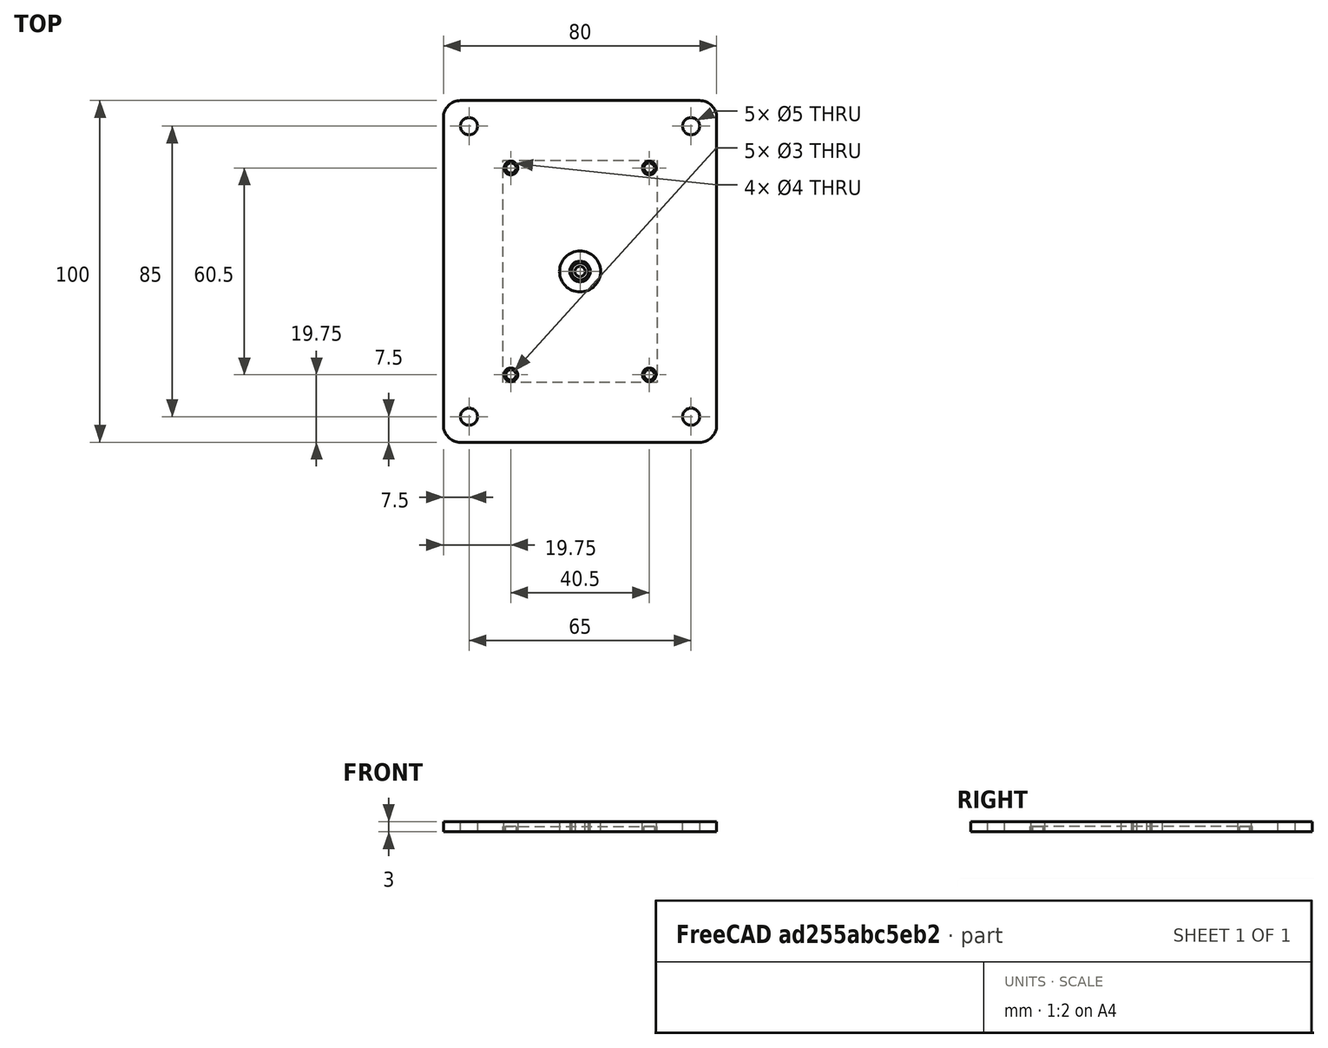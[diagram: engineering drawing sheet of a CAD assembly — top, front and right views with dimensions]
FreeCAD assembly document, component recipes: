
FREECAD ASSEMBLY — COMPONENT RECIPES ("ttgo_esp32_poe_mounting_plate")

This assembly document has 4 components, labeled P0..P3 below (a component is one placed body or linked part). 4 of them carry a construction recipe — the FreeCAD feature program that regenerates the part from scratch, quoted from this document or its linked companion documents; the rest are supplied as boundary geometry only. No exploded tour is included for this assembly.
COMPONENT P0 — recipe-attached ("Mounting Panel", modeled in this document).
Construction recipe (the document's own serialized feature program — sketch geometry with constraints, then the solid features built on it; lengths are millimeters unless a unit is written):

FEATURE [Sketcher::SketchObject] Sketch
  FullyConstrained = true
  MapMode = 5
  Support = -> [XY_Plane002]
  sketch-geometry (12):
    g0: LineSegment StartX=-40 StartY=50 StartZ=0 EndX=40 EndY=50 EndZ=0
    g1: LineSegment StartX=40 StartY=50 StartZ=0 EndX=40 EndY=-50 EndZ=0
    g2: LineSegment StartX=40 StartY=-50 StartZ=0 EndX=-40 EndY=-50 EndZ=0
    g3: LineSegment StartX=-40 StartY=-50 StartZ=0 EndX=-40 EndY=50 EndZ=0
    g4: LineSegment StartX=-35 StartY=50 StartZ=0 EndX=35 EndY=50 EndZ=0
    g5: LineSegment StartX=40 StartY=45 StartZ=0 EndX=40 EndY=-45 EndZ=0
    g6: LineSegment StartX=35 StartY=-50 StartZ=0 EndX=-35 EndY=-50 EndZ=0
    g7: LineSegment StartX=-40 StartY=-45 StartZ=0 EndX=-40 EndY=45 EndZ=0
    g8: ArcOfCircle CenterX=-35 CenterY=45 CenterZ=0 NormalX=0 NormalY=0 NormalZ=1 AngleXU=0 Radius=5 StartAngle=1.5708 EndAngle=3.14159
    g9: ArcOfCircle CenterX=35 CenterY=45 CenterZ=0 NormalX=0 NormalY=0 NormalZ=1 AngleXU=0 Radius=5 StartAngle=0 EndAngle=1.5708
    g10: ArcOfCircle CenterX=35 CenterY=-45 CenterZ=0 NormalX=0 NormalY=0 NormalZ=1 AngleXU=0 Radius=5 StartAngle=4.71239 EndAngle=6.28319
    g11: ArcOfCircle CenterX=-35 CenterY=-45 CenterZ=0 NormalX=0 NormalY=0 NormalZ=1 AngleXU=0 Radius=5 StartAngle=3.14159 EndAngle=4.71239
  constraints (30):
    c: Coincident(g0,g1)
    c: Coincident(g1,g2)
    c: Coincident(g2,g3)
    c: Coincident(g3,g0)
    c: Horizontal(g2)
    c: Vertical(g3)
    c: Symmetric(g0,g0,g-2)
    c: Symmetric(g0,g1,g-1)
    c: DistanceX(g0,g0) = 80
    c: DistanceY(g1,g1) = 100
    c: Horizontal(g4)
    c: Horizontal(g6)
    c: Vertical(g5)
    c: Vertical(g7)
    c: Tangent(g4,g8) = 1.5708
    c: Tangent(g7,g8) = 1.5708
    c: Tangent(g4,g9) = 1.5708
    c: Tangent(g5,g9) = 1.5708
    c: Tangent(g5,g10) = 1.5708
    c: Tangent(g6,g10) = 1.5708
    c: Tangent(g7,g11) = 1.5708
    c: Tangent(g6,g11) = 1.5708
    c: PointOnObject(g4,g0)
    c: PointOnObject(g7,g3)
    c: PointOnObject(g5,g1)
    c: PointOnObject(g6,g2)
    c: Equal(g8,g9)
    c: Equal(g9,g11)
    c: Equal(g11,g10)
    c: Radius(g11) = 5
FEATURE [PartDesign::Plane] DatumPlane001
  AttachmentOffset = pos=(0,0,3) rot=(0,0,1;0rad)
  Length = 97.8885
  MapMode = 5
  Placement = pos=(0,0,3) rot=(0,0,1;0rad)
  ResizeMode = 0
  Support = -> [XY_Plane002]
  Width = 117.889
FEATURE [PartDesign::Pad] Pad001
  Direction = (0,0,1)
  Length = 10
  Length2 = 10
  Profile = -> Sketch
  ReferenceAxis = -> Sketch [N_Axis]
  Type = 3
  UpToFace = -> DatumPlane001 [Plane]
FEATURE [Sketcher::SketchObject] Sketch003
  FullyConstrained = true
  MapMode = 5
  Placement = pos=(0,0,3) rot=(0,0,1;0rad)
  Support = -> [DatumPlane001]
  sketch-geometry (8):
    g0: LineSegment StartX=-20.25 StartY=30.25 StartZ=0 EndX=20.25 EndY=30.25 EndZ=0
    g1: LineSegment StartX=20.25 StartY=30.25 StartZ=0 EndX=20.25 EndY=-30.25 EndZ=0
    g2: LineSegment StartX=20.25 StartY=-30.25 StartZ=0 EndX=-20.25 EndY=-30.25 EndZ=0
    g3: LineSegment StartX=-20.25 StartY=-30.25 StartZ=0 EndX=-20.25 EndY=30.25 EndZ=0
    g4: Circle CenterX=-20.25 CenterY=30.25 CenterZ=0 NormalX=0 NormalY=0 NormalZ=1 AngleXU=0 Radius=2
    g5: Circle CenterX=20.25 CenterY=30.25 CenterZ=0 NormalX=0 NormalY=0 NormalZ=1 AngleXU=0 Radius=2
    g6: Circle CenterX=-20.25 CenterY=-30.25 CenterZ=0 NormalX=0 NormalY=0 NormalZ=1 AngleXU=0 Radius=2
    g7: Circle CenterX=20.25 CenterY=-30.25 CenterZ=0 NormalX=0 NormalY=0 NormalZ=1 AngleXU=0 Radius=2
  constraints (18):
    c: Coincident(g0,g1)
    c: Coincident(g1,g2)
    c: Coincident(g2,g3)
    c: Coincident(g3,g0)
    c: Horizontal(g2)
    c: Vertical(g3)
    c: Coincident(g4,g0)
    c: Coincident(g5,g0)
    c: Coincident(g6,g2)
    c: Coincident(g7,g1)
    c: Equal(g4,g5)
    c: Equal(g5,g6)
    c: Equal(g6,g7)
    c: Diameter(g6) = 4
    c: Symmetric(g4,g5,g-2)
    c: Symmetric(g5,g7,g-1)
    c: DistanceX(g0,g0) = 40.5
    c: DistanceY(g1,g1) = 60.5
FEATURE [PartDesign::Pocket] Pocket001
  BaseFeature = -> Pad001
  Direction = (0,0,-1)
  Length = 0
  Length2 = 5
  Profile = -> Sketch003
  ReferenceAxis = -> Sketch003 [N_Axis]
  Type = 3
  UpToFace = -> XY_Plane002
FEATURE [PartDesign::CoordinateSystem] Local_CS001  label="Mounting Panel Body Lower Left TTGO Board Mounting Hole"
  AttacherType = Attacher::AttachEngine3D
  MapMode = 45
  Placement = pos=(-20.25,-30.25,3) rot=(0,0,-1;1e-05rad)
  Support = -> [Pocket001]
FEATURE [Sketcher::SketchObject] Sketch004
  FullyConstrained = true
  MapMode = 5
  Placement = pos=(0,0,3) rot=(0,0,1;0rad)
  Support = -> [DatumPlane001]
  sketch-geometry (8):
    g0: LineSegment StartX=-32.5 StartY=42.5 StartZ=0 EndX=32.5 EndY=42.5 EndZ=0
    g1: LineSegment StartX=32.5 StartY=42.5 StartZ=0 EndX=32.5 EndY=-42.5 EndZ=0
    g2: LineSegment StartX=32.5 StartY=-42.5 StartZ=0 EndX=-32.5 EndY=-42.5 EndZ=0
    g3: LineSegment StartX=-32.5 StartY=-42.5 StartZ=0 EndX=-32.5 EndY=42.5 EndZ=0
    g4: Circle CenterX=-32.5 CenterY=42.5 CenterZ=0 NormalX=0 NormalY=0 NormalZ=1 AngleXU=0 Radius=2.5
    g5: Circle CenterX=32.5 CenterY=42.5 CenterZ=0 NormalX=0 NormalY=0 NormalZ=1 AngleXU=0 Radius=2.5
    g6: Circle CenterX=-32.5 CenterY=-42.5 CenterZ=0 NormalX=0 NormalY=0 NormalZ=1 AngleXU=0 Radius=2.5
    g7: Circle CenterX=32.5 CenterY=-42.5 CenterZ=0 NormalX=0 NormalY=0 NormalZ=1 AngleXU=0 Radius=2.5
  constraints (18):
    c: Coincident(g0,g1)
    c: Coincident(g1,g2)
    c: Coincident(g2,g3)
    c: Coincident(g3,g0)
    c: Horizontal(g2)
    c: Vertical(g3)
    c: Symmetric(g0,g0,g-2)
    c: Symmetric(g0,g1,g-1)
    c: Coincident(g4,g0)
    c: Coincident(g5,g0)
    c: Coincident(g6,g2)
    c: Coincident(g7,g1)
    c: Equal(g4,g5)
    c: Equal(g5,g6)
    c: Equal(g6,g7)
    c: Diameter(g6) = 5
    c: DistanceX(g0,g0) = 65
    c: DistanceY(g1,g1) = 85
FEATURE [PartDesign::Pocket] Pocket002
  BaseFeature = -> Pocket001
  Direction = (0,0,-1)
  Length = 0
  Length2 = 5
  Profile = -> Sketch004
  ReferenceAxis = -> Sketch004 [N_Axis]
  Type = 3
  UpToFace = -> XY_Plane002
FEATURE [PartDesign::CoordinateSystem] Local_CS004  label="Mounting Panel Body Lower Left Mounting Hole"
  AttacherType = Attacher::AttachEngine3D
  MapMode = 45
  Placement = pos=(-32.5,-42.5,0) rot=(0,0,-1;1.1e-05rad)
  Support = -> [Pocket002]
FEATURE [PartDesign::Body] Body
  Group = -> [Sketch,DatumPlane001,Pad001,Sketch003,Pocket001,Local_CS001,Sketch004,Pocket002,Local_CS004]
  Origin = -> Origin002
  Tip = -> Pocket002
COMPONENT P1 — recipe-attached ("Mounting Panel Mounting Spacer", modeled in this document).
Construction recipe (the document's own serialized feature program — sketch geometry with constraints, then the solid features built on it; lengths are millimeters unless a unit is written):

FEATURE [Sketcher::SketchObject] Sketch006
  FullyConstrained = true
  MapMode = 5
  Support = -> [XY_Plane008]
  sketch-geometry (2):
    g0: Circle CenterX=0 CenterY=0 CenterZ=0 NormalX=0 NormalY=0 NormalZ=1 AngleXU=0 Radius=2.5
    g1: Circle CenterX=0 CenterY=0 CenterZ=0 NormalX=0 NormalY=0 NormalZ=1 AngleXU=0 Radius=6
  constraints (4):
    c: Coincident(g0,g-1)
    c: Coincident(g1,g0)
    c: Diameter(g0) = 5
    c: Diameter(g1) = 12
FEATURE [PartDesign::Pad] Pad003
  Direction = (0,0,1)
  Length = 3
  Length2 = 10
  Profile = -> Sketch006
  ReferenceAxis = -> Sketch006 [N_Axis]
  Type = 0
FEATURE [PartDesign::CoordinateSystem] Local_CS005  label="Mounting Panel Mounting Spacer Body Upper"
  AttacherType = Attacher::AttachEngine3D
  MapMode = 45
  Placement = pos=(1.19e-14,1e-16,3) rot=(0,0,1;0rad)
  Support = -> [Pad003]
FEATURE [PartDesign::CoordinateSystem] Local_CS006  label="Mounting Panel Mounting Spacer Body Lower"
  AttacherType = Attacher::AttachEngine3D
  MapMode = 45
  Placement = pos=(1.19e-14,1e-16,0) rot=(0,0,1;0rad)
  Support = -> [Pad003]
FEATURE [PartDesign::Body] Body_4
  Group = -> [Sketch006,Pad003,Local_CS005,Local_CS006]
  Origin = -> Origin008
  Tip = -> Pad003
COMPONENT P2 — recipe-attached ("TTGO Board", modeled in this document).
Construction recipe (the document's own serialized feature program — sketch geometry with constraints, then the solid features built on it; lengths are millimeters unless a unit is written):

FEATURE [Sketcher::SketchObject] Sketch001
  FullyConstrained = true
  MapMode = 5
  Support = -> [XY_Plane004]
  sketch-geometry (4):
    g0: LineSegment StartX=-22.5 StartY=32.5 StartZ=0 EndX=22.5 EndY=32.5 EndZ=0
    g1: LineSegment StartX=22.5 StartY=32.5 StartZ=0 EndX=22.5 EndY=-32.5 EndZ=0
    g2: LineSegment StartX=22.5 StartY=-32.5 StartZ=0 EndX=-22.5 EndY=-32.5 EndZ=0
    g3: LineSegment StartX=-22.5 StartY=-32.5 StartZ=0 EndX=-22.5 EndY=32.5 EndZ=0
  constraints (10):
    c: Coincident(g0,g1)
    c: Coincident(g1,g2)
    c: Coincident(g2,g3)
    c: Coincident(g3,g0)
    c: Horizontal(g2)
    c: Vertical(g3)
    c: DistanceX(g0,g0) = 45
    c: DistanceY(g1,g1) = 65
    c: Symmetric(g0,g0,g-2)
    c: Symmetric(g0,g1,g-1)
FEATURE [PartDesign::Plane] DatumPlane
  AttachmentOffset = pos=(0,0,1.6) rot=(0,0,1;0rad)
  Length = 61.4018
  MapMode = 5
  Placement = pos=(0,0,1.6) rot=(0,0,1;0rad)
  ResizeMode = 0
  Support = -> [XY_Plane004]
  Width = 76.4018
FEATURE [PartDesign::Pad] Pad
  Direction = (0,0,1)
  Length = 1.6
  Length2 = 10
  Profile = -> Sketch001
  ReferenceAxis = -> Sketch001 [N_Axis]
  Type = 3
  UpToFace = -> DatumPlane [Plane]
FEATURE [Sketcher::SketchObject] Sketch002
  FullyConstrained = true
  MapMode = 5
  Placement = pos=(0,0,1.6) rot=(0,0,1;0rad)
  Support = -> [DatumPlane]
  sketch-geometry (8):
    g0: LineSegment StartX=-20.25 StartY=30.25 StartZ=0 EndX=20.25 EndY=30.25 EndZ=0
    g1: LineSegment StartX=20.25 StartY=30.25 StartZ=0 EndX=20.25 EndY=-30.25 EndZ=0
    g2: LineSegment StartX=20.25 StartY=-30.25 StartZ=0 EndX=-20.25 EndY=-30.25 EndZ=0
    g3: LineSegment StartX=-20.25 StartY=-30.25 StartZ=0 EndX=-20.25 EndY=30.25 EndZ=0
    g4: Circle CenterX=-20.25 CenterY=30.25 CenterZ=0 NormalX=0 NormalY=0 NormalZ=1 AngleXU=0 Radius=1.5
    g5: Circle CenterX=20.25 CenterY=30.25 CenterZ=0 NormalX=0 NormalY=0 NormalZ=1 AngleXU=0 Radius=1.5
    g6: Circle CenterX=20.25 CenterY=-30.25 CenterZ=0 NormalX=0 NormalY=0 NormalZ=1 AngleXU=0 Radius=1.5
    g7: Circle CenterX=-20.25 CenterY=-30.25 CenterZ=0 NormalX=0 NormalY=0 NormalZ=1 AngleXU=0 Radius=1.5
  constraints (18):
    c: Coincident(g0,g1)
    c: Coincident(g1,g2)
    c: Coincident(g2,g3)
    c: Coincident(g3,g0)
    c: Horizontal(g2)
    c: Vertical(g3)
    c: Symmetric(g0,g0,g-2)
    c: Symmetric(g0,g1,g-1)
    c: DistanceX(g0,g0) = 40.5
    c: DistanceY(g1,g1) = 60.5
    c: Coincident(g4,g0)
    c: Coincident(g5,g0)
    c: Coincident(g6,g1)
    c: Coincident(g7,g2)
    c: Equal(g4,g5)
    c: Equal(g5,g6)
    c: Equal(g6,g7)
    c: Diameter(g7) = 3
FEATURE [PartDesign::Pocket] Pocket
  BaseFeature = -> Pad
  Direction = (0,0,-1)
  Length = 0
  Length2 = 5
  Profile = -> Sketch002
  ReferenceAxis = -> Sketch002 [N_Axis]
  Type = 3
  UpToFace = -> XY_Plane004
FEATURE [PartDesign::CoordinateSystem] Local_CS  label="TTGO Board Body Lower Left Mounting Hole"
  AttacherType = Attacher::AttachEngine3D
  MapMode = 45
  Placement = pos=(-20.25,-30.25,0) rot=(0,0,1;1.2e-05rad)
  Support = -> [Pocket]
FEATURE [PartDesign::Body] Body_2
  Group = -> [DatumPlane,Sketch001,Pad,Sketch002,Pocket,Local_CS]
  Origin = -> Origin004
  Tip = -> Pocket
COMPONENT P3 — recipe-attached ("TTGO Board Mounting Spacer", modeled in this document).
Construction recipe (the document's own serialized feature program — sketch geometry with constraints, then the solid features built on it; lengths are millimeters unless a unit is written):

FEATURE [Sketcher::SketchObject] Sketch005
  FullyConstrained = true
  MapMode = 5
  Support = -> [XY_Plane006]
  sketch-geometry (2):
    g0: Circle CenterX=0 CenterY=0 CenterZ=0 NormalX=0 NormalY=0 NormalZ=1 AngleXU=0 Radius=3
    g1: Circle CenterX=0 CenterY=0 CenterZ=0 NormalX=0 NormalY=0 NormalZ=1 AngleXU=0 Radius=1.5
  constraints (4):
    c: Coincident(g0,g-1)
    c: Coincident(g1,g0)
    c: Diameter(g0) = 6
    c: Diameter(g1) = 3
FEATURE [PartDesign::Pad] Pad002
  Direction = (0,0,1)
  Length = 3
  Length2 = 10
  Profile = -> Sketch005
  ReferenceAxis = -> Sketch005 [N_Axis]
  Type = 0
FEATURE [PartDesign::CoordinateSystem] Local_CS002  label="TTGO Board Mounting Spacer Body Upper"
  AttacherType = Attacher::AttachEngine3D
  MapMode = 45
  Placement = pos=(7.1e-15,1e-16,3) rot=(0,0,1;0rad)
  Support = -> [Pad002]
FEATURE [PartDesign::CoordinateSystem] Local_CS003  label="TTGO Board Mounting Spacer Body Lower"
  AttacherType = Attacher::AttachEngine3D
  MapMode = 45
  Placement = pos=(7.1e-15,1e-16,0) rot=(0,0,1;0rad)
  Support = -> [Pad002]
FEATURE [PartDesign::Body] Body_3
  Group = -> [Sketch005,Pad002,Local_CS002,Local_CS003]
  Origin = -> Origin006
  Tip = -> Pad002
PROVENANCE & LICENSES
A FreeCAD (.FCStd) document from a public repository crawl; recipes are the document's own serialized feature recipes (and, for linked parts, companion documents' recipes).
License: as declared in the source repository (recorded in the dataset sidecar).
